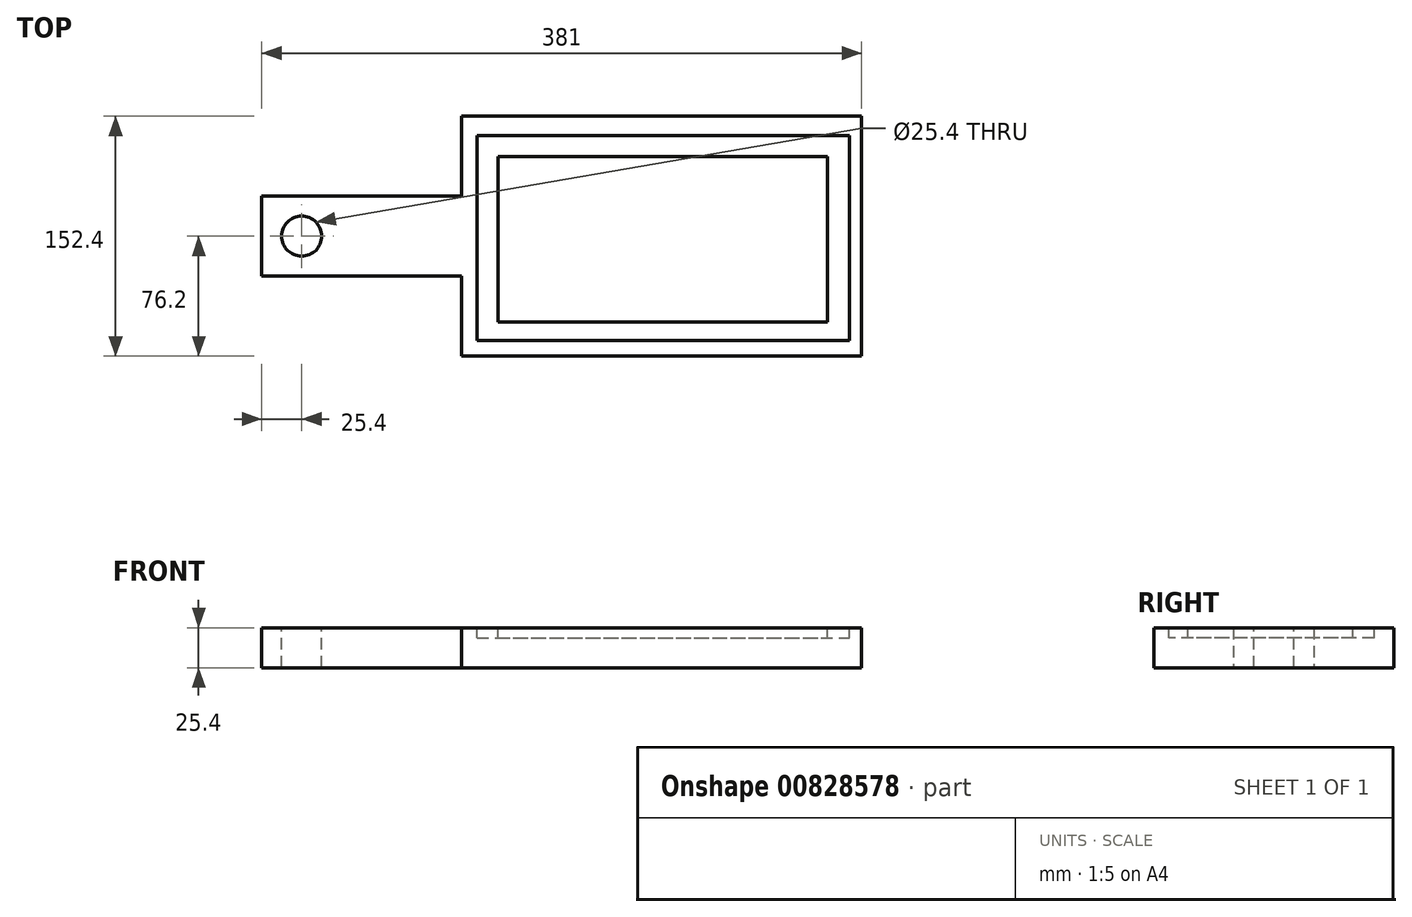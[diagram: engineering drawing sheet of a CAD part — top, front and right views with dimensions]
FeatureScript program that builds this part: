
annotation { "Feature Type Name" : "Feature", "Feature Type Description" : "" }
export const myFeature = defineFeature(function(context is Context, id is Id, definition is map)
    precondition{}
    {
        {
            var Q0;
            Q0=qCreatedBy(makeId("Top.planeOp"),FACE);
            var sketch = newSketch(context, id + "F0", { "sketchPlane" : qUnion([Q0])});
            skLineSegment(sketch, "E0.bottom", {"start": v(0, 0) * mm, "end": v(254, 0) * mm});
            skLineSegment(sketch, "E0.top", {"start": v(0, 152.4) * mm, "end": v(254, 152.4) * mm});
            skLineSegment(sketch, "E0.left", {"start": v(0, 0) * mm, "end": v(0, 152.4) * mm});
            skLineSegment(sketch, "E0.right", {"start": v(254, 0) * mm, "end": v(254, 152.4) * mm});
            skLineSegment(sketch, "E1.bottom", {"start": v(0, 101.6) * mm, "end": v(-127, 101.6) * mm});
            skLineSegment(sketch, "E1.top", {"start": v(0, 50.8) * mm, "end": v(-127, 50.8) * mm});
            skLineSegment(sketch, "E1.left", {"start": v(0, 101.6) * mm, "end": v(0, 50.8) * mm});
            skLineSegment(sketch, "E1.right", {"start": v(-127, 101.6) * mm, "end": v(-127, 50.8) * mm});
            skSolve(sketch);
        }
        {
            var Q0;
            Q0 = qSketchRegion(id + "F0", true);
            extrude(context, id + "F1", {"entities" : qUnion([Q0]), "depth" : 25.4 * mm, "offsetDistance" : 25.4 * mm});
        }
        {
            var Q0;
            Q0=makeQuery(id+"F1.opExtrude","CAP_FACE",FACE,{"disambiguationData":[OSD([sQuery(id+"F0.wireOp",EDGE,"E0.bottom"),sQuery(id+"F0.wireOp",EDGE,"E0.top"),sQuery(id+"F0.wireOp",EDGE,"E0.left"),sQuery(id+"F0.wireOp",EDGE,"E0.right"),sQuery(id+"F0.wireOp",EDGE,"E1.bottom"),sQuery(id+"F0.wireOp",EDGE,"E1.top"),sQuery(id+"F0.wireOp",EDGE,"E1.right")])],"isStart":false});
            var sketch = newSketch(context, id + "F2", { "sketchPlane" : qUnion([Q0])});
            skCircle(sketch, "E2", {"center": v(-101.6, 76.2) * mm, "radius": 12.7 * mm});
            skSolve(sketch);
        }
        {
            var Q0;
            Q0=makeQuery(id+"F2.imprint","IMPRINT",FACE,{"disambiguationData":[TD([[makeQuery(id+"F2.imprint","IMPRINT",EDGE,{"derivedFrom":sQuery(id+"F2.wireOp",EDGE,"E2")}),1.0]])]});
            extrude(context, id + "F3", {"entities" : qUnion([Q0]), "operationType" : NewBodyOperationType.REMOVE, "oppositeDirection" : true, "depth" : 25.4 * mm, "offsetDistance" : 25.4 * mm});
        }
        {
            var Q0;
            Q0=makeQuery(id+"F1.opExtrude","CAP_FACE",FACE,{"disambiguationData":[OSD([sQuery(id+"F0.wireOp",EDGE,"E0.bottom"),sQuery(id+"F0.wireOp",EDGE,"E0.top"),sQuery(id+"F0.wireOp",EDGE,"E0.left"),sQuery(id+"F0.wireOp",EDGE,"E0.right"),sQuery(id+"F0.wireOp",EDGE,"E1.bottom"),sQuery(id+"F0.wireOp",EDGE,"E1.top"),sQuery(id+"F0.wireOp",EDGE,"E1.right")])],"isStart":false});
            var sketch = newSketch(context, id + "F4", { "sketchPlane" : qUnion([Q0])});
            skLineSegment(sketch, "E3.bottom", {"start": v(9.67, 140.17) * mm, "end": v(246.25, 140.17) * mm});
            skLineSegment(sketch, "E3.top", {"start": v(9.67, 9.82) * mm, "end": v(246.25, 9.82) * mm});
            skLineSegment(sketch, "E3.left", {"start": v(9.67, 140.17) * mm, "end": v(9.67, 9.82) * mm});
            skLineSegment(sketch, "E3.right", {"start": v(246.25, 140.17) * mm, "end": v(246.25, 9.82) * mm});
            skLineSegment(sketch, "E4.bottom", {"start": v(23.16, 126.68) * mm, "end": v(232.18, 126.68) * mm});
            skLineSegment(sketch, "E4.top", {"start": v(23.16, 21.6) * mm, "end": v(232.18, 21.6) * mm});
            skLineSegment(sketch, "E4.left", {"start": v(23.16, 126.68) * mm, "end": v(23.16, 21.6) * mm});
            skLineSegment(sketch, "E4.right", {"start": v(232.18, 126.68) * mm, "end": v(232.18, 21.6) * mm});
            skSolve(sketch);
        }
        {
            var Q0;
            Q0 = qSketchRegion(id + "F4", true);
            extrude(context, id + "F5", {"entities" : qUnion([Q0]), "operationType" : NewBodyOperationType.REMOVE, "oppositeDirection" : true, "depth" : 6.35 * mm, "offsetDistance" : 25.4 * mm});
        }
    });
